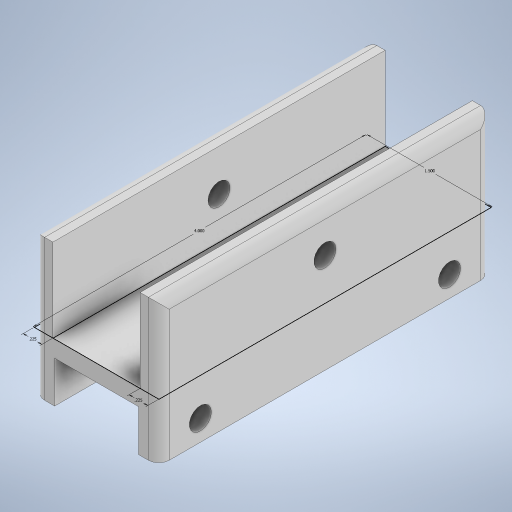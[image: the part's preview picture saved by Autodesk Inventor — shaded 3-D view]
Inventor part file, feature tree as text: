
AUTODESK INVENTOR PART (.ipt)
format: ipt  version: 2024.1 (Build 281209000, 209)  size: 279,040 bytes
history: native  units: in
note: dims shown in document units (in); Inventor stores cm internally (conversion verified against a paired STEP export)
features: extrude x3, hole x2, sketch x2, fillet x1
ambient origin geometry x8: Origin, YZ Plane, XZ Plane, XY Plane, X Axis, Y Axis, Z Axis, Center Point
bodies: Solid1 (feature_tree)
feature tree (8):
  extrude  "Extrusion1"  Depth=4.0in
  extrude  "Extrusion2"  Depth=0.225in
  hole  "Hole1"  [1 undecoded]
  extrude  "Extrusion3"  Depth=0.2in TaperAngle=0.0deg
  hole  "Hole2"  [1 undecoded]
  fillet  "Fillet1"  Radius=0.245in
  sketch  "Sketch3"  dims[d0=1.5in d1=4.0in]
  sketch  "Sketch4"  dims[d2=0.225in d3=0.225in d4=1.0in d5=0.0in d6=0.2in d7=0.0in d8=0.5in d9=0.266in d10=0.75in d11=0.438in d12=0.25in d13=0.5635in d14=1.0in d15=0.8108in d16=0.245in d17=4.0in d18=0.245in d19=0.5in d20=0.0in d21=0.5in d22=0.25in d23=0.5in d24=0.266in d25=0.043in d26=0.438in d27=0.25in d28=0.5635in d29=1.0in d30=0.8108in d31=0.125in]
note: 2 required parameter values undecoded (feature->parameter linkage not recoverable at this tier; creation-order binding heuristic only, values carry confidence <= 0.55)
